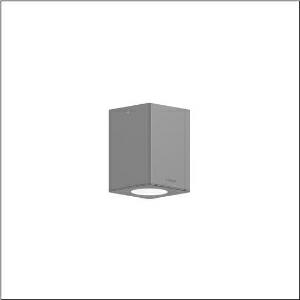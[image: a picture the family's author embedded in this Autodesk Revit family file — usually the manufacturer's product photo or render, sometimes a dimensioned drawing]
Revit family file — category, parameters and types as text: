
# Revit family: cl_31_decke_5cl613603
name_source: partatom
category: Lighting Fixtures
units: mm (PartAtom-declared; Revit-internal decimal feet)

## family parameters
Cut with Voids When Loaded = No
Host = Face
Light Source = No
Part Type = Normal
Room Calculation Point = No
Round Connector Dimension = Use Diameter
Shared = No

## types (1)
- --- (1 x LED, 1500 lm, 15 W, 3000K)
    Apparent Load = 15 VA
    CIE Flux Codes = 98 100 100 100 100
    Color Rendering = 80
    Color Temperature = 3000K
    Default Elevation = 1800 mm
    Description = CL 31 Ceiling, ceiling luminaire, primary light control with reflector, of aluminium, primary optical cover: cover panel, of glass, transparent, primary light characteristic: symmetric, installation type: surface-mounted, LED, rated luminous flux: 1.500lm, luminous efficacy: 100lm/W, light colour: 830, colour temperature: 3000K, control gear: DALI, with terminal, 5-pole, max. 2.5mm², mains connection: 220..240V, AC, 50/60Hz, rated input power: 15W, luminaire housing, of aluminium, powder-coated, Siteco® metallic grey, length: 120mm, width: 120mm, height: 165mm, protection rating (complete): IP65, insulation class (complete): insulation class I (protective earthing), certification: CE, ENEC, impact resistance: IK09, permissible operating ambient temperature for outdoor applications: -20..+50°C, packaging unit: 1 piece
    Height = 166 mm
    Lamp = 1 x LED
    Lamp Light Flux = 1500 lm
    Lamp Power = 15 W
    Lamp count = 1
    Length = 120 mm
    Luminous efficacy = 100 lm/W
    Manufacturer = Siteco
    ModVariant = No
    Model = 5CL613603
    Mounting Place = Ceiling
    Mounting Type = Surface mounted
    Number of Poles = 1
    OnlyDefault = Yes
    Power Factor = 1
    Product Name = CL 31 Decke
    Product group = ceiling luminaire
    ProductGroupID = 307
    Protection Class = Protection class I
    Protection Degree = IP 65
    RLX_Detail_Level = 1
    RLX_Emergency_Light_Flux = 0 lm
    RLX_Emergency_Type = 0
    RLX_Emergency_Type_DB = No
    RlxData = <blob elided: 33249 chars, md5=325c6bee>
    Socket = socket
    Standby Power = 0 W
    System Light Flux = 1500 lm
    System Power = 15 W
    Type Comments = factory setting: luminous flux: 100 % | dim-lin: 254 | 348 mA
    Type Image = l_1006909.jpg
    URL = http://relux.com
    VarID = @adj_195476
    Voltage = 0 V
    Weight = 0.00 kg
    Width = 120 mm

## geometry (parser evidence)
native form markers: Blend x4, Sweep x10
no freeform markers — native parametric forms only
